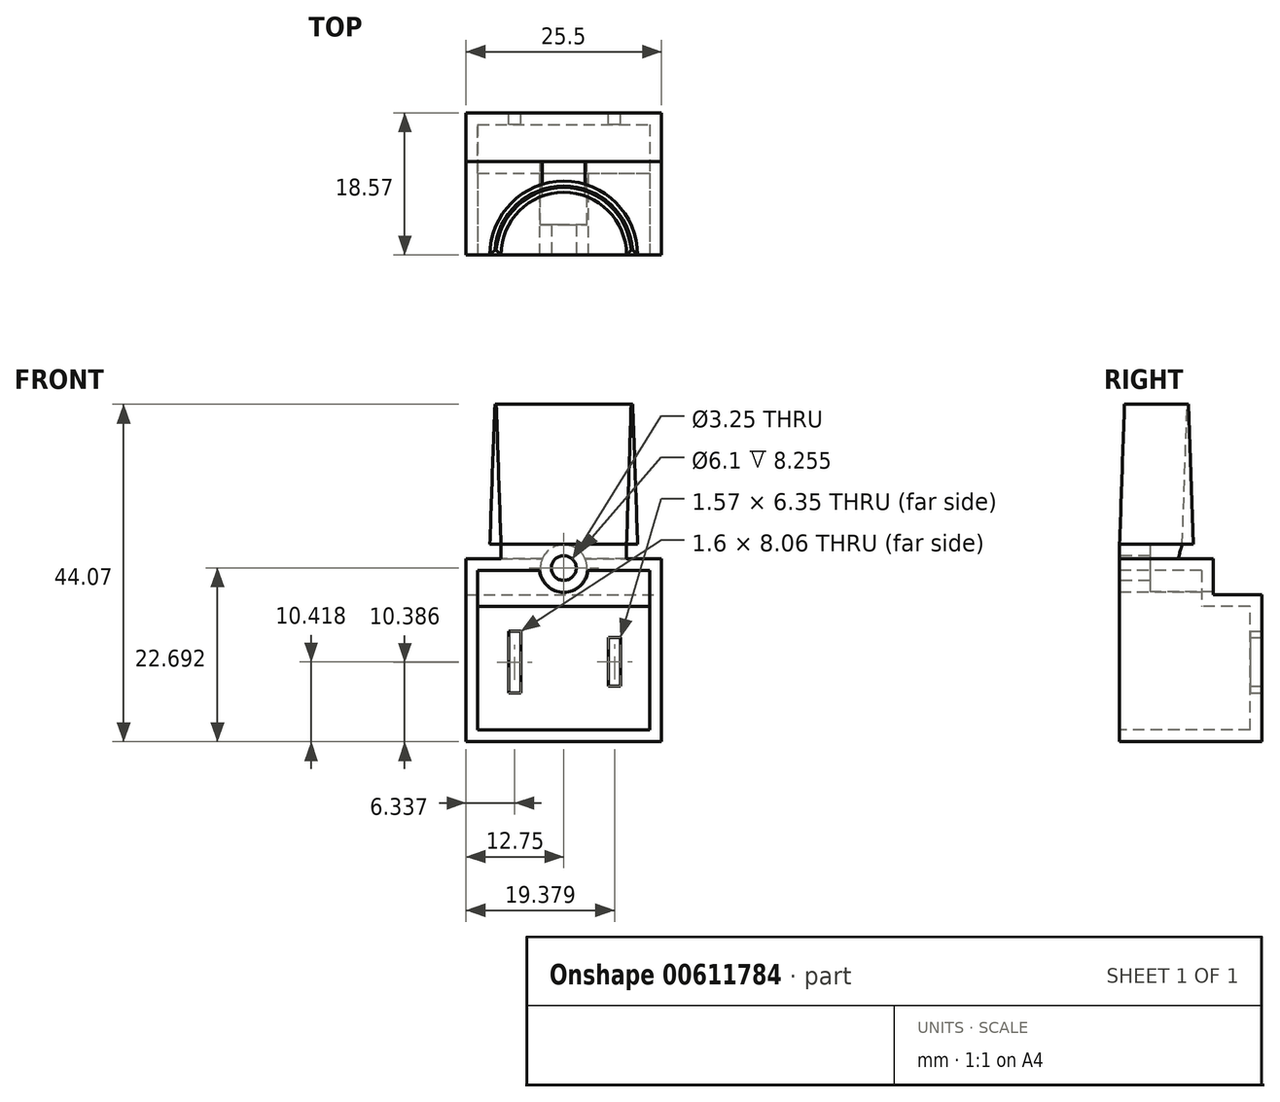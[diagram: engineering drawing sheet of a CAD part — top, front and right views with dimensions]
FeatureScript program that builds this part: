
annotation { "Feature Type Name" : "Feature", "Feature Type Description" : "" }
export const myFeature = defineFeature(function(context is Context, id is Id, definition is map)
    precondition{}
    {
        {
            var Q0;
            Q0=qCreatedBy(makeId("Front.planeOp"),FACE);
            var sketch = newSketch(context, id + "F0", { "sketchPlane" : qUnion([Q0])});
            skLineSegment(sketch, "E0.bottom", {"start": v(-12.75, -23.88) * mm, "end": v(12.75, -23.88) * mm});
            skLineSegment(sketch, "E0.top", {"start": v(-12.75, 0) * mm, "end": v(12.75, 0) * mm});
            skLineSegment(sketch, "E0.left", {"start": v(-12.75, -23.88) * mm, "end": v(-12.75, 0) * mm});
            skLineSegment(sketch, "E0.right", {"start": v(12.75, -23.88) * mm, "end": v(12.75, 0) * mm});
            skSolve(sketch);
        }
        {
            var Q0;
            Q0=makeQuery(id+"F0.imprint","IMPRINT",FACE,{"disambiguationData":[TD([[makeQuery(id+"F0.imprint","IMPRINT",EDGE,{"derivedFrom":sQuery(id+"F0.wireOp",EDGE,"E0.bottom")}),1.0]])]});
            extrude(context, id + "F1", {"entities" : qUnion([Q0]), "oppositeDirection" : true, "depth" : 18.57 * mm, "offsetDistance" : 25.4 * mm});
        }
        {
            var Q0;
            Q0=makeQuery(id+"F1.opExtrude","SWEPT_FACE",FACE,{"disambiguationData":[OSD([sQuery(id+"F0.wireOp",EDGE,"E0.right")])]});
            var sketch = newSketch(context, id + "F2", { "sketchPlane" : qUnion([Q0])});
            skLineSegment(sketch, "E1.bottom", {"start": v(18.57, 0) * mm, "end": v(12.22, 0) * mm});
            skLineSegment(sketch, "E1.top", {"start": v(18.57, -4.7) * mm, "end": v(12.22, -4.7) * mm});
            skLineSegment(sketch, "E1.left", {"start": v(18.57, 0) * mm, "end": v(18.57, -4.7) * mm});
            skLineSegment(sketch, "E1.right", {"start": v(12.22, 0) * mm, "end": v(12.22, -4.7) * mm});
            skSolve(sketch);
        }
        {
            var Q0;
            Q0=makeQuery(id+"F2.imprint","IMPRINT",FACE,{"disambiguationData":[TD([[makeQuery(id+"F2.imprint","IMPRINT",EDGE,{"derivedFrom":sQuery(id+"F2.wireOp",EDGE,"E1.bottom")}),1.0]])]});
            extrude(context, id + "F3", {"entities" : qUnion([Q0]), "operationType" : NewBodyOperationType.REMOVE, "endBound" : BoundingType.UP_TO_NEXT, "oppositeDirection" : true, "depth" : 25.4 * mm, "offsetDistance" : 25.4 * mm});
        }
        {
            var Q0;
            Q0=makeQuery(id+"F1.opExtrude","CAP_FACE",FACE,{"disambiguationData":[OSD([sQuery(id+"F0.wireOp",EDGE,"E0.bottom"),sQuery(id+"F0.wireOp",EDGE,"E0.top"),sQuery(id+"F0.wireOp",EDGE,"E0.left"),sQuery(id+"F0.wireOp",EDGE,"E0.right")])],"isStart":true});
            shell(context, id + "F4", {"entities" : qUnion([Q0]), "thickness" : 1.52 * mm});
        }
        {
            var Q0;
            Q0=makeQuery(id+"F1.opExtrude","SWEPT_FACE",FACE,{"disambiguationData":[OSD([sQuery(id+"F0.wireOp",EDGE,"E0.top")])]});
            var sketch = newSketch(context, id + "F5", { "sketchPlane" : qUnion([Q0])});
            skArc(sketch, "E2", {"start": v(8.2, 0) * mm, "mid": v(0, 8.2) * mm, "end": v(-8.2, 0) * mm});
            skLineSegment(sketch, "E3", {"start": v(-8.2, 0) * mm, "end": v(8.2, 0) * mm});
            skSolve(sketch);
        }
        {
            var Q0;
            Q0=makeQuery(id+"F5.imprint","IMPRINT",FACE,{"disambiguationData":[TD([[makeQuery(id+"F5.imprint","IMPRINT",EDGE,{"derivedFrom":sQuery(id+"F5.wireOp",EDGE,"E2")}),1.0]])]});
            extrude(context, id + "F6", {"entities" : qUnion([Q0]), "operationType" : NewBodyOperationType.ADD, "depth" : 1.9 * mm, "offsetDistance" : 25.4 * mm});
        }
        {
            var Q0;
            Q0=makeQuery(id+"F6.opExtrude","CAP_FACE",FACE,{"disambiguationData":[OSD([sQuery(id+"F5.wireOp",EDGE,"E2"),sQuery(id+"F5.wireOp",EDGE,"E3")])],"isStart":false});
            var sketch = newSketch(context, id + "F7", { "sketchPlane" : qUnion([Q0])});
            skArc(sketch, "E4", {"start": v(9.65, 0) * mm, "mid": v(0, 9.65) * mm, "end": v(-9.65, 0) * mm});
            skLineSegment(sketch, "E5", {"start": v(-9.65, 0) * mm, "end": v(9.65, 0) * mm});
            skSolve(sketch);
        }
        {
            var Q0;
            {var subQ0=sQuery(id+"F7.wireOp",EDGE,"E4");Q0=makeQuery(id+"F7.imprint","IMPRINT",FACE,{"disambiguationData":[TD([[makeQuery(id+"F7.imprint","IMPRINT",EDGE,{"derivedFrom":subQ0}),1.0]])]});}
            extrude(context, id + "F8", {"entities" : qUnion([Q0]), "depth" : 18.8 * mm, "offsetDistance" : 25.4 * mm, "hasDraft" : true, "draftAngle" : 3 * degree, "draftPullDirection" : true});
        }
        {
            var Q0;
            {var subQ0=sQuery(id+"F7.wireOp",EDGE,"E4");Q0=makeQuery(id+"F7.imprint","IMPRINT",FACE,{"disambiguationData":[TD([[makeQuery(id+"F7.imprint","IMPRINT",EDGE,{"derivedFrom":subQ0}),1.0]])]});}
            extrude(context, id + "F9", {"entities" : qUnion([Q0]), "operationType" : NewBodyOperationType.ADD, "depth" : 18.29 * mm, "offsetDistance" : 25.4 * mm, "hasDraft" : true, "draftAngle" : 2 * degree, "draftPullDirection" : true});
        }
        {
            var Q0;
            Q0=makeQuery(id+"F6.boolean.opBoolean","MERGE",FACE,{"derivedFrom":[makeQuery(id+"F1.opExtrude","CAP_FACE",FACE,{"disambiguationData":[OSD([sQuery(id+"F0.wireOp",EDGE,"E0.bottom"),sQuery(id+"F0.wireOp",EDGE,"E0.top"),sQuery(id+"F0.wireOp",EDGE,"E0.left"),sQuery(id+"F0.wireOp",EDGE,"E0.right")])],"isStart":true}),makeQuery(id+"F6.opExtrude","SWEPT_FACE",FACE,{"disambiguationData":[OSD([sQuery(id+"F5.wireOp",EDGE,"E3")])]})]});
            var sketch = newSketch(context, id + "F10", { "sketchPlane" : qUnion([Q0])});
            skCircle(sketch, "E6", {"center": v(0, -1.19) * mm, "radius": 3.17 * mm});
            skSolve(sketch);
        }
        {
            var Q0;
            Q0 = qSketchRegion(id + "F10", true);
            extrude(context, id + "F11", {"entities" : qUnion([Q0]), "operationType" : NewBodyOperationType.ADD, "endBound" : BoundingType.UP_TO_NEXT, "oppositeDirection" : true, "depth" : 25.4 * mm, "offsetDistance" : 25.4 * mm});
        }
        {
            var Q0;
            Q0=makeQuery(id+"F11.boolean.opBoolean","MERGE",FACE,{"derivedFrom":[makeQuery(id+"F6.boolean.opBoolean","MERGE",FACE,{"derivedFrom":[makeQuery(id+"F1.opExtrude","CAP_FACE",FACE,{"disambiguationData":[OSD([sQuery(id+"F0.wireOp",EDGE,"E0.bottom"),sQuery(id+"F0.wireOp",EDGE,"E0.top"),sQuery(id+"F0.wireOp",EDGE,"E0.left"),sQuery(id+"F0.wireOp",EDGE,"E0.right")])],"isStart":true}),makeQuery(id+"F6.opExtrude","SWEPT_FACE",FACE,{"disambiguationData":[OSD([sQuery(id+"F5.wireOp",EDGE,"E3")])]})]}),makeQuery(id+"F11.opExtrude","CAP_FACE",FACE,{"disambiguationData":[OSD([sQuery(id+"F10.wireOp",EDGE,"E6")])],"isStart":true})]});
            var sketch = newSketch(context, id + "F12", { "sketchPlane" : qUnion([Q0])});
            skCircle(sketch, "E7", {"center": v(0, -1.19) * mm, "radius": 1.62 * mm});
            skSolve(sketch);
        }
        {
            var Q0;
            Q0=makeQuery(id+"F12.imprint","IMPRINT",FACE,{"disambiguationData":[TD([[makeQuery(id+"F12.imprint","IMPRINT",EDGE,{"derivedFrom":sQuery(id+"F12.wireOp",EDGE,"E7")}),1.0]])]});
            extrude(context, id + "F13", {"entities" : qUnion([Q0]), "operationType" : NewBodyOperationType.REMOVE, "endBound" : BoundingType.UP_TO_NEXT, "oppositeDirection" : true, "depth" : 25.4 * mm, "offsetDistance" : 25.4 * mm});
        }
        {
            var Q0;
            Q0=makeQuery(id+"F3.boolean.opBoolean","COPY",FACE,{"derivedFrom":makeQuery(id+"F3.opExtrude","SWEPT_FACE",FACE,{"disambiguationData":[OSD([sQuery(id+"F2.wireOp",EDGE,"E1.right")])]})});
            var sketch = newSketch(context, id + "F14", { "sketchPlane" : qUnion([Q0])});
            skCircle(sketch, "E8", {"center": v(0, -1.19) * mm, "radius": 3.05 * mm});
            skSolve(sketch);
        }
        {
            var Q0;
            Q0 = qSketchRegion(id + "F14", true);
            var Q1;
            Q1=sQuery(id+"F14.wireOp",EDGE,"E8");
            extrude(context, id + "F15", {"entities" : qUnion([Q0]), "operationType" : NewBodyOperationType.REMOVE, "surfaceEntities" : qUnion([Q1]), "oppositeDirection" : true, "depth" : 8.25 * mm, "offsetDistance" : 25.4 * mm});
        }
        {
            var Q0;
            Q0=makeQuery(id+"F1.opExtrude","CAP_FACE",FACE,{"disambiguationData":[OSD([sQuery(id+"F0.wireOp",EDGE,"E0.bottom"),sQuery(id+"F0.wireOp",EDGE,"E0.top"),sQuery(id+"F0.wireOp",EDGE,"E0.left"),sQuery(id+"F0.wireOp",EDGE,"E0.right")])],"isStart":false});
            var sketch = newSketch(context, id + "F16", { "sketchPlane" : qUnion([Q0])});
            skLineSegment(sketch, "E9.bottom", {"start": v(5.61, -9.46) * mm, "end": v(7.21, -9.46) * mm});
            skLineSegment(sketch, "E9.top", {"start": v(5.61, -17.53) * mm, "end": v(7.21, -17.53) * mm});
            skLineSegment(sketch, "E9.left", {"start": v(5.61, -9.46) * mm, "end": v(5.61, -17.53) * mm});
            skLineSegment(sketch, "E9.right", {"start": v(7.21, -9.46) * mm, "end": v(7.21, -17.53) * mm});
            skLineSegment(sketch, "E10.bottom", {"start": v(-7.42, -10.29) * mm, "end": v(-5.84, -10.29) * mm});
            skLineSegment(sketch, "E10.top", {"start": v(-7.42, -16.64) * mm, "end": v(-5.84, -16.64) * mm});
            skLineSegment(sketch, "E10.left", {"start": v(-7.42, -10.29) * mm, "end": v(-7.42, -16.64) * mm});
            skLineSegment(sketch, "E10.right", {"start": v(-5.84, -10.29) * mm, "end": v(-5.84, -16.64) * mm});
            skSolve(sketch);
        }
        {
            var Q0;
            Q0 = qSketchRegion(id + "F16", true);
            extrude(context, id + "F17", {"entities" : qUnion([Q0]), "operationType" : NewBodyOperationType.REMOVE, "endBound" : BoundingType.UP_TO_NEXT, "oppositeDirection" : true, "depth" : 25.4 * mm, "offsetDistance" : 25.4 * mm});
        }
    });
